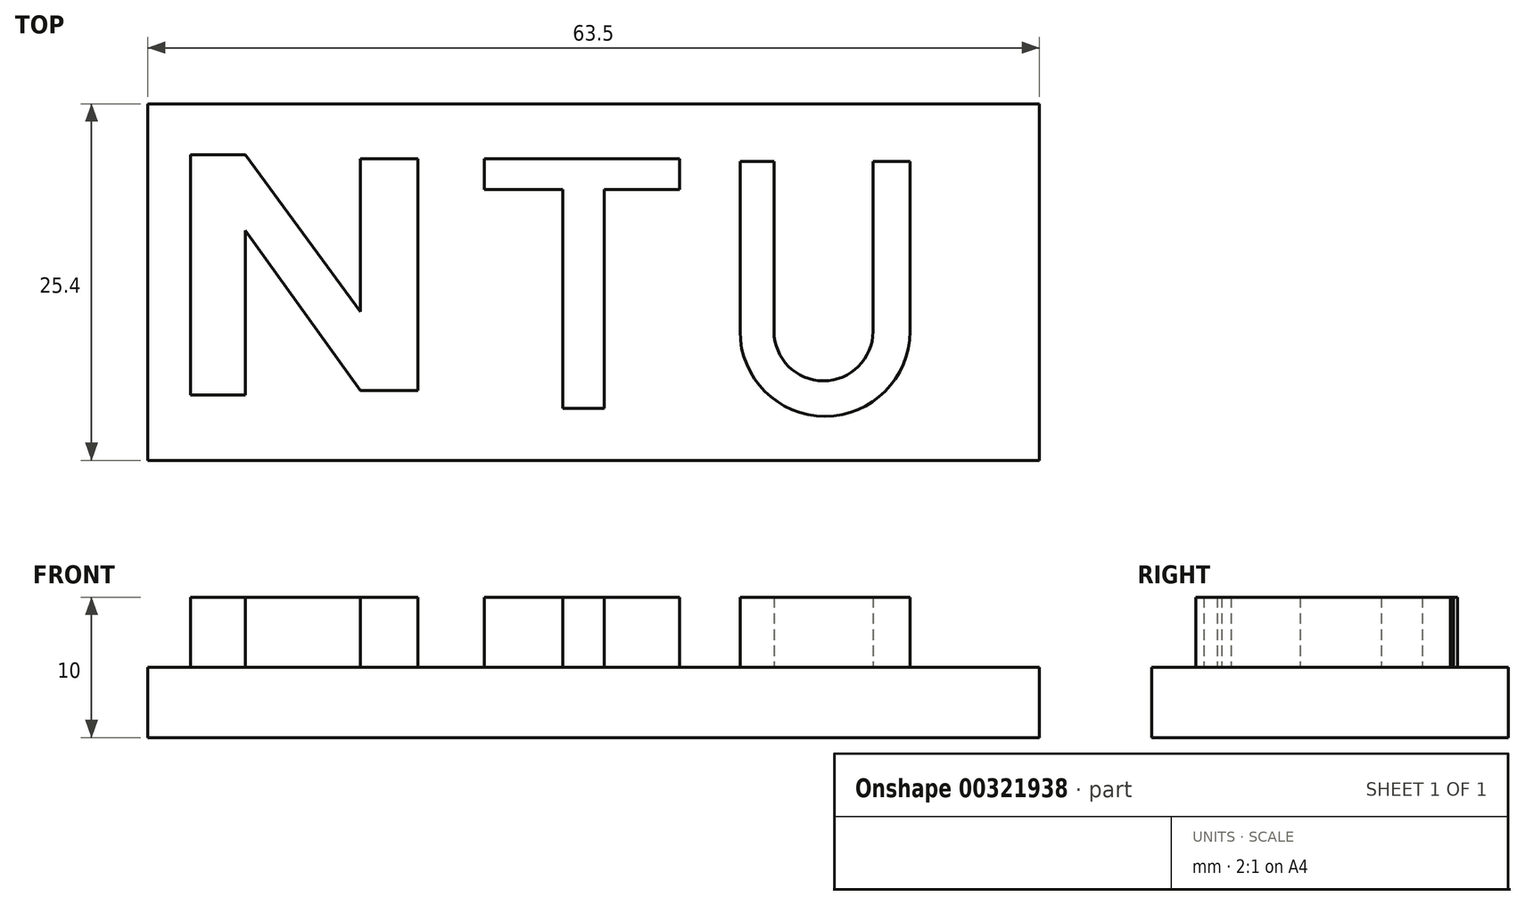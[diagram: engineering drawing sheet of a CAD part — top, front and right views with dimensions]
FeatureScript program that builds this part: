
annotation { "Feature Type Name" : "Feature", "Feature Type Description" : "" }
export const myFeature = defineFeature(function(context is Context, id is Id, definition is map)
    precondition{}
    {
        {
            var Q0;
            Q0=qCreatedBy(makeId("Top.planeOp"),FACE);
            var sketch = newSketch(context, id + "F0", { "sketchPlane" : qUnion([Q0])});
            skLineSegment(sketch, "E0.bottom", {"start": v(-31.75, -12.7) * mm, "end": v(31.75, -12.7) * mm});
            skLineSegment(sketch, "E0.top", {"start": v(-31.75, 12.7) * mm, "end": v(31.75, 12.7) * mm});
            skLineSegment(sketch, "E0.left", {"start": v(-31.75, -12.7) * mm, "end": v(-31.75, 12.7) * mm});
            skLineSegment(sketch, "E0.right", {"start": v(31.75, -12.7) * mm, "end": v(31.75, 12.7) * mm});
            skPoint(sketch, "E0.middle", {"position": v(0, 0) * mm});
            skSolve(sketch);
        }
        {
            var Q0;
            Q0 = qSketchRegion(id + "F0", true);
            extrude(context, id + "F1", {"entities" : qUnion([Q0]), "depth" : 5 * mm});
        }
        {
            var Q0;
            Q0=makeQuery(id+"F1.opExtrude","CAP_FACE",FACE,{"disambiguationData":[OSD([sQuery(id+"F0.wireOp",EDGE,"E0.bottom"),sQuery(id+"F0.wireOp",EDGE,"E0.top"),sQuery(id+"F0.wireOp",EDGE,"E0.left"),sQuery(id+"F0.wireOp",EDGE,"E0.right")])],"isStart":false});
            var sketch = newSketch(context, id + "F2", { "sketchPlane" : qUnion([Q0])});
            skLineSegment(sketch, "E1.bottom", {"start": v(-28.7, 9.07) * mm, "end": v(-24.8, 9.07) * mm});
            skLineSegment(sketch, "E1.top", {"start": v(-28.7, -8.04) * mm, "end": v(-24.8, -8.04) * mm});
            skLineSegment(sketch, "E1.left", {"start": v(-28.7, 9.07) * mm, "end": v(-28.7, -8.04) * mm});
            skLineSegment(sketch, "E1.right", {"start": v(-24.8, 3.66) * mm, "end": v(-24.8, -8.04) * mm});
            skLineSegment(sketch, "E2.bottom", {"start": v(-16.6, 8.79) * mm, "end": v(-12.5, 8.79) * mm});
            skLineSegment(sketch, "E2.top", {"start": v(-16.6, -7.73) * mm, "end": v(-12.5, -7.73) * mm});
            skLineSegment(sketch, "E2.left", {"start": v(-12.5, 8.79) * mm, "end": v(-12.5, -7.73) * mm});
            skLineSegment(sketch, "E2.right", {"start": v(-16.6, 8.79) * mm, "end": v(-16.6, -2.13) * mm});
            skLineSegment(sketch, "E3.bottom", {"start": v(-7.77, 8.79) * mm, "end": v(6.12, 8.79) * mm});
            skLineSegment(sketch, "E3.top", {"start": v(-7.77, 6.58) * mm, "end": v(-2.2, 6.58) * mm});
            skLineSegment(sketch, "E3.left", {"start": v(-7.77, 8.79) * mm, "end": v(-7.77, 6.58) * mm});
            skLineSegment(sketch, "E3.right", {"start": v(6.12, 8.79) * mm, "end": v(6.12, 6.58) * mm});
            skLineSegment(sketch, "E4.bottom", {"start": v(-2.2, 8.79) * mm, "end": v(0.75, 8.79) * mm});
            skLineSegment(sketch, "E4.top", {"start": v(-2.2, -8.99) * mm, "end": v(0.75, -8.99) * mm});
            skLineSegment(sketch, "E4.left", {"start": v(-2.2, 6.58) * mm, "end": v(-2.2, -8.99) * mm});
            skLineSegment(sketch, "E4.right", {"start": v(0.75, 6.58) * mm, "end": v(0.75, -8.99) * mm});
            skLineSegment(sketch, "E5", {"start": v(-24.8, 3.66) * mm, "end": v(-16.6, -7.73) * mm});
            skLineSegment(sketch, "E6", {"start": v(-24.8, 9.07) * mm, "end": v(-16.6, -2.13) * mm});
            skLineSegment(sketch, "E7.bottom", {"start": v(10.43, 8.58) * mm, "end": v(12.85, 8.58) * mm});
            skLineSegment(sketch, "E7.left", {"start": v(10.43, 8.58) * mm, "end": v(10.43, -3.52) * mm});
            skLineSegment(sketch, "E7.right", {"start": v(12.85, 8.58) * mm, "end": v(12.85, -3.52) * mm});
            skLineSegment(sketch, "E8.bottom", {"start": v(19.9, 8.58) * mm, "end": v(22.53, 8.58) * mm});
            skLineSegment(sketch, "E8.left", {"start": v(19.9, 8.58) * mm, "end": v(19.9, -3.52) * mm});
            skLineSegment(sketch, "E8.right", {"start": v(22.53, 8.58) * mm, "end": v(22.53, -3.52) * mm});
            skLineSegment(sketch, "E9", {"start": v(12.85, -3.52) * mm, "end": v(19.9, -3.52) * mm, "construction": true});
            skArc(sketch, "E10", {"start": v(19.9, -3.52) * mm, "mid": v(16.38, -7.04) * mm, "end": v(12.85, -3.52) * mm});
            skArc(sketch, "E11", {"start": v(22.53, -3.52) * mm, "mid": v(16.48, -9.57) * mm, "end": v(10.43, -3.52) * mm});
            skLineSegment(sketch, "E12.trimOffspring", {"start": v(0.75, 6.58) * mm, "end": v(6.12, 6.58) * mm});
            skLineSegment(sketch, "E13.trimOffspring", {"start": v(22.53, -3.52) * mm, "end": v(31.75, -3.52) * mm, "construction": true});
            skSolve(sketch);
        }
        {
            var Q0;
            Q0 = qSketchRegion(id + "F2", true);
            extrude(context, id + "F3", {"entities" : qUnion([Q0]), "operationType" : NewBodyOperationType.ADD, "depth" : 5 * mm});
        }
    });
